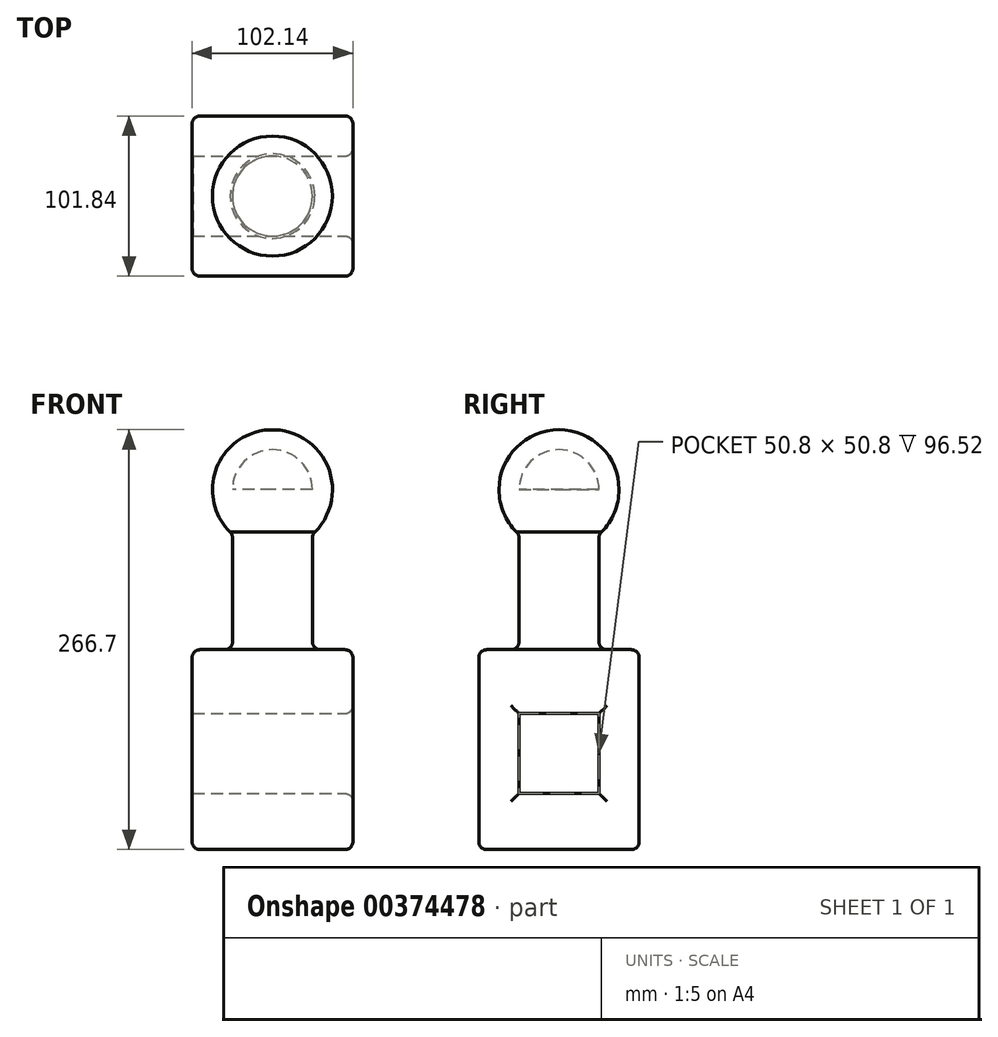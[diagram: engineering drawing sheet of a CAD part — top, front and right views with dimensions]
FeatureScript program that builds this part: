
annotation { "Feature Type Name" : "Feature", "Feature Type Description" : "" }
export const myFeature = defineFeature(function(context is Context, id is Id, definition is map)
    precondition{}
    {
        {
            var Q0;
            Q0=qCreatedBy(makeId("Top.planeOp"),FACE);
            var sketch = newSketch(context, id + "F0", { "sketchPlane" : qUnion([Q0])});
            skLineSegment(sketch, "E0.bottom", {"start": v(51.07, -50.92) * mm, "end": v(-51.07, -50.92) * mm});
            skLineSegment(sketch, "E0.top", {"start": v(51.07, 50.92) * mm, "end": v(-51.07, 50.92) * mm});
            skLineSegment(sketch, "E0.left", {"start": v(51.07, -50.92) * mm, "end": v(51.07, 50.92) * mm});
            skLineSegment(sketch, "E0.right", {"start": v(-51.07, -50.92) * mm, "end": v(-51.07, 50.92) * mm});
            skPoint(sketch, "E0.middle", {"position": v(0, 0) * mm});
            skSolve(sketch);
        }
        {
            var Q0;
            Q0 = qSketchRegion(id + "F0", true);
            extrude(context, id + "F1", {"entities" : qUnion([Q0]), "depth" : 101.6 * mm});
        }
        {
            var Q0;
            Q0=makeQuery(id+"F1.opExtrude","CAP_FACE",FACE,{"disambiguationData":[OSD([sQuery(id+"F0.wireOp",EDGE,"E0.bottom"),sQuery(id+"F0.wireOp",EDGE,"E0.top"),sQuery(id+"F0.wireOp",EDGE,"E0.left"),sQuery(id+"F0.wireOp",EDGE,"E0.right")])],"isStart":false});
            extrude(context, id + "F2", {"entities" : qUnion([Q0]), "operationType" : NewBodyOperationType.ADD, "depth" : 25.4 * mm});
        }
        {
            var Q0;
            Q0=makeQuery(id+"F2.opExtrude","CAP_FACE",FACE,{"disambiguationData":[OSD([sQuery(id+"F0.wireOp",EDGE,"E0.bottom"),sQuery(id+"F0.wireOp",EDGE,"E0.top"),sQuery(id+"F0.wireOp",EDGE,"E0.left"),sQuery(id+"F0.wireOp",EDGE,"E0.right")])],"isStart":false});
            var sketch = newSketch(context, id + "F3", { "sketchPlane" : qUnion([Q0])});
            skCircle(sketch, "E1", {"center": v(0, 0) * mm, "radius": 25.4 * mm});
            skSolve(sketch);
        }
        {
            var Q0;
            Q0 = qSketchRegion(id + "F3", true);
            extrude(context, id + "F4", {"entities" : qUnion([Q0]), "operationType" : NewBodyOperationType.ADD, "depth" : 101.6 * mm});
        }
        {
            var Q0;
            Q0=makeQuery(id+"F4.opExtrude","CAP_FACE",FACE,{"disambiguationData":[OSD([sQuery(id+"F3.wireOp",EDGE,"E1")])],"isStart":false});
            var sketch = newSketch(context, id + "F5", { "sketchPlane" : qUnion([Q0])});
            skArc(sketch, "E2", {"start": v(0, -38.1) * mm, "mid": v(38.1, 0) * mm, "end": v(0, 38.1) * mm});
            skLineSegment(sketch, "E3", {"start": v(0, 38.1) * mm, "end": v(0, -38.1) * mm});
            skSolve(sketch);
        }
        {
            var Q0;
            {var subQ0=sQuery(id+"F5.wireOp",EDGE,"E2");Q0=makeQuery(id+"F5.imprint","IMPRINT",FACE,{"disambiguationData":[TD([[makeQuery(id+"F5.imprint","IMPRINT",EDGE,{"derivedFrom":subQ0}),1.0]])]});}
            var Q1;
            Q1=sQuery(id+"F5.wireOp",EDGE,"E3");
            revolve(context, id + "F6", {"operationType" : NewBodyOperationType.ADD, "entities" : qUnion([Q0]), "axis" : qUnion([Q1]), "revolveType" : RevolveType.FULL});
        }
        {
            var Q0;
            {var subQ0=sQuery(id+"F0.wireOp",EDGE,"E0.left");Q0=makeQuery(id+"F2.boolean.opBoolean","MERGE",FACE,{"derivedFrom":[makeQuery(id+"F1.opExtrude","SWEPT_FACE",FACE,{"disambiguationData":[OSD([subQ0])]}),makeQuery(id+"F2.opExtrude","SWEPT_FACE",FACE,{"disambiguationData":[OSD([subQ0])]})]});}
            var sketch = newSketch(context, id + "F7", { "sketchPlane" : qUnion([Q0])});
            skLineSegment(sketch, "E4.bottom", {"start": v(25.4, 35.6) * mm, "end": v(-25.4, 35.6) * mm});
            skLineSegment(sketch, "E4.top", {"start": v(25.4, 86.4) * mm, "end": v(-25.4, 86.4) * mm});
            skLineSegment(sketch, "E4.left", {"start": v(25.4, 35.6) * mm, "end": v(25.4, 86.4) * mm});
            skLineSegment(sketch, "E4.right", {"start": v(-25.4, 35.6) * mm, "end": v(-25.4, 86.4) * mm});
            skPoint(sketch, "E4.middle", {"position": v(0, 61) * mm});
            skSolve(sketch);
        }
        {
            var Q0;
            Q0=makeQuery(id+"F7.imprint","IMPRINT",FACE,{"disambiguationData":[TD([[makeQuery(id+"F7.imprint","IMPRINT",EDGE,{"derivedFrom":sQuery(id+"F7.wireOp",EDGE,"E4.bottom")}),-1.0]])]});
            extrude(context, id + "F8", {"entities" : qUnion([Q0]), "operationType" : NewBodyOperationType.REMOVE, "oppositeDirection" : true, "depth" : 101.6 * mm});
        }
        {
            var Q0;
            Q0=makeQuery(id+"F2.opExtrude","CAP_EDGE",EDGE,{"disambiguationData":[OSD([sQuery(id+"F0.wireOp",EDGE,"E0.top")])],"isStart":false});
            var Q1;
            {var subQ0=sQuery(id+"F0.wireOp",EDGE,"E0.left");var subQ1=sQuery(id+"F0.wireOp",EDGE,"E0.top");Q1=makeQuery(id+"F2.boolean.opBoolean","MERGE",EDGE,{"derivedFrom":[makeQuery(id+"F1.opExtrude","SWEPT_EDGE",EDGE,{"disambiguationData":[OSD([subQ1,subQ0])]}),makeQuery(id+"F2.opExtrude","SWEPT_EDGE",EDGE,{"disambiguationData":[OSD([subQ1,subQ0])]})]});}
            var Q2;
            {var subQ0=sQuery(id+"F0.wireOp",EDGE,"E0.top");Q2=makeQuery(id+"F2.boolean.opBoolean","MERGE",FACE,{"derivedFrom":[makeQuery(id+"F1.opExtrude","SWEPT_FACE",FACE,{"disambiguationData":[OSD([subQ0])]}),makeQuery(id+"F2.opExtrude","SWEPT_FACE",FACE,{"disambiguationData":[OSD([subQ0])]})]});}
            var Q3;
            {var subQ0=sQuery(id+"F0.wireOp",EDGE,"E0.right");var subQ1=sQuery(id+"F0.wireOp",EDGE,"E0.top");Q3=makeQuery(id+"F2.boolean.opBoolean","MERGE",EDGE,{"derivedFrom":[makeQuery(id+"F1.opExtrude","SWEPT_EDGE",EDGE,{"disambiguationData":[OSD([subQ1,subQ0])]}),makeQuery(id+"F2.opExtrude","SWEPT_EDGE",EDGE,{"disambiguationData":[OSD([subQ1,subQ0])]})]});}
            var Q4;
            Q4=makeQuery(id+"F2.opExtrude","CAP_EDGE",EDGE,{"disambiguationData":[OSD([sQuery(id+"F0.wireOp",EDGE,"E0.left")])],"isStart":false});
            var Q5;
            {var subQ0=sQuery(id+"F0.wireOp",EDGE,"E0.left");Q5=makeQuery(id+"F2.boolean.opBoolean","MERGE",FACE,{"derivedFrom":[makeQuery(id+"F1.opExtrude","SWEPT_FACE",FACE,{"disambiguationData":[OSD([subQ0])]}),makeQuery(id+"F2.opExtrude","SWEPT_FACE",FACE,{"disambiguationData":[OSD([subQ0])]})]});}
            var Q6;
            {var subQ0=sQuery(id+"F0.wireOp",EDGE,"E0.left");var subQ1=sQuery(id+"F0.wireOp",EDGE,"E0.bottom");Q6=makeQuery(id+"F2.boolean.opBoolean","MERGE",EDGE,{"derivedFrom":[makeQuery(id+"F1.opExtrude","SWEPT_EDGE",EDGE,{"disambiguationData":[OSD([subQ1,subQ0])]}),makeQuery(id+"F2.opExtrude","SWEPT_EDGE",EDGE,{"disambiguationData":[OSD([subQ1,subQ0])]})]});}
            var Q7;
            Q7=makeQuery(id+"F1.opExtrude","CAP_EDGE",EDGE,{"disambiguationData":[OSD([sQuery(id+"F0.wireOp",EDGE,"E0.right")])],"isStart":true});
            var Q8;
            Q8=makeQuery(id+"F1.opExtrude","CAP_EDGE",EDGE,{"disambiguationData":[OSD([sQuery(id+"F0.wireOp",EDGE,"E0.bottom")])],"isStart":true});
            var Q9;
            Q9=makeQuery(id+"F2.opExtrude","CAP_EDGE",EDGE,{"disambiguationData":[OSD([sQuery(id+"F0.wireOp",EDGE,"E0.bottom")])],"isStart":false});
            var Q10;
            Q10=makeQuery(id+"F2.opExtrude","CAP_EDGE",EDGE,{"disambiguationData":[OSD([sQuery(id+"F0.wireOp",EDGE,"E0.right")])],"isStart":false});
            var Q11;
            {var subQ0=sQuery(id+"F0.wireOp",EDGE,"E0.right");var subQ1=sQuery(id+"F0.wireOp",EDGE,"E0.bottom");Q11=makeQuery(id+"F2.boolean.opBoolean","MERGE",EDGE,{"derivedFrom":[makeQuery(id+"F1.opExtrude","SWEPT_EDGE",EDGE,{"disambiguationData":[OSD([subQ1,subQ0])]}),makeQuery(id+"F2.opExtrude","SWEPT_EDGE",EDGE,{"disambiguationData":[OSD([subQ1,subQ0])]})]});}
            var Q12;
            Q12=makeQuery(id+"F6.boolean.opBoolean","INTERSECT",EDGE,{"derivedFrom":[makeQuery(id+"F4.opExtrude","SWEPT_FACE",FACE,{"disambiguationData":[OSD([sQuery(id+"F3.wireOp",EDGE,"E1")])]}),makeQuery(id+"F6.opRevolve","SWEPT_FACE",FACE,{"disambiguationData":[OSD([sQuery(id+"F5.wireOp",EDGE,"E2")])]})]});
            var Q13;
            Q13=makeQuery(id+"F4.opExtrude","SWEPT_FACE",FACE,{"disambiguationData":[OSD([sQuery(id+"F3.wireOp",EDGE,"E1")])]});
            fillet(context, id + "F9", {"entities" : qUnion([Q0, Q1, Q2, Q3, Q4, Q5, Q6, Q7, Q8, Q9, Q10, Q11, Q12, Q13]), "radius" : 5.08 * mm, "tangentPropagation" : true, "allowEdgeOverflow" : false});
        }
    });
